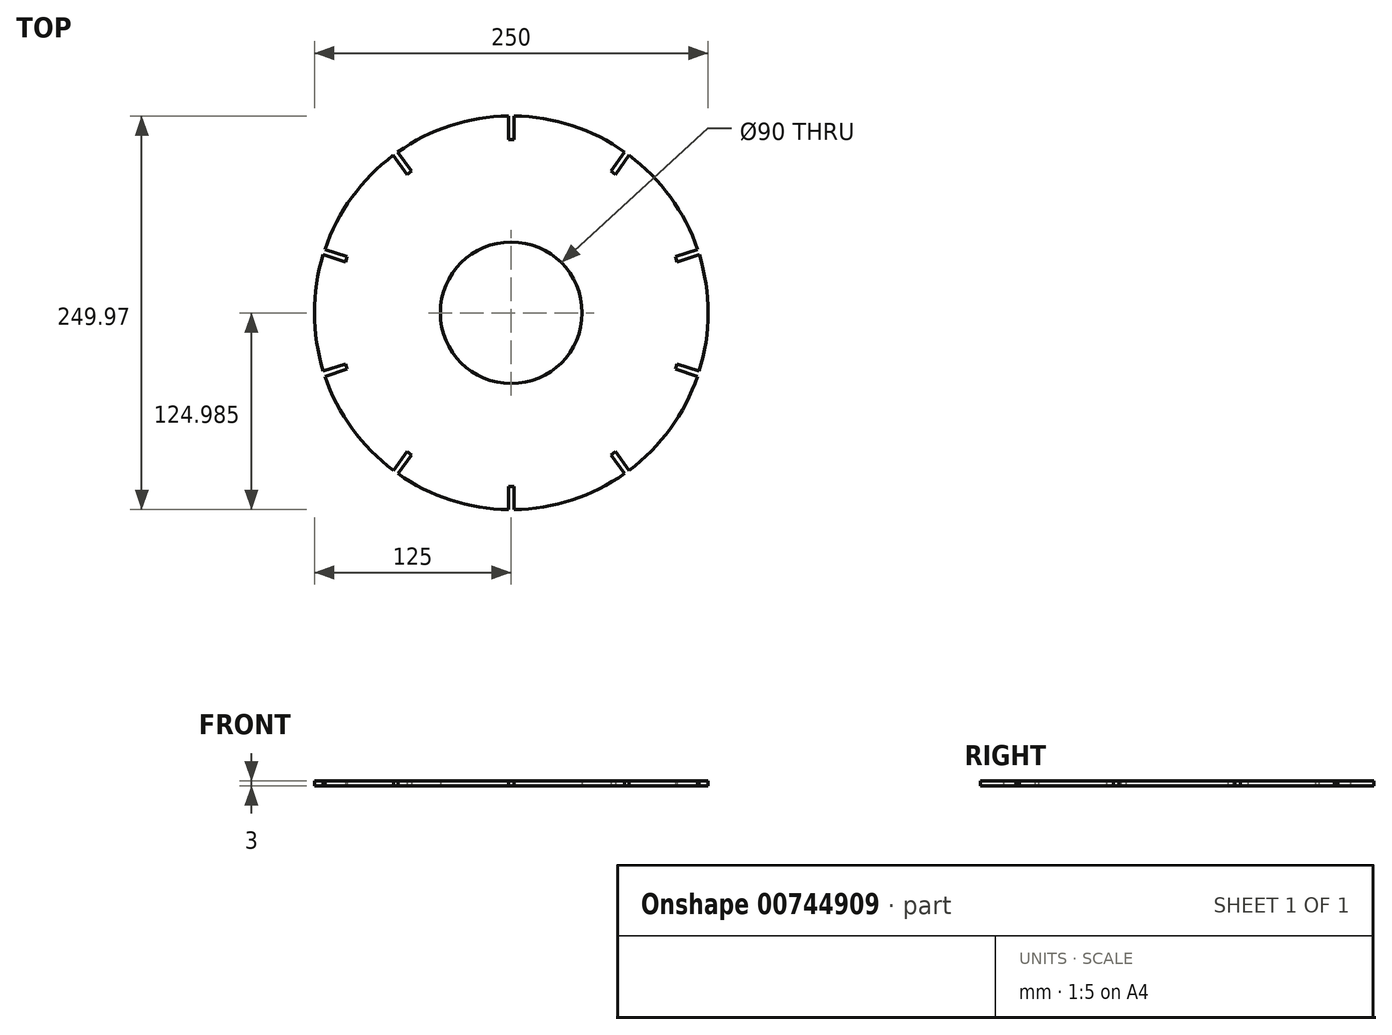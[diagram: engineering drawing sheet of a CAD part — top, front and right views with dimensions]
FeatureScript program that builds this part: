
annotation { "Feature Type Name" : "Feature", "Feature Type Description" : "" }
export const myFeature = defineFeature(function(context is Context, id is Id, definition is map)
    precondition{}
    {
        {
            var Q0;
            Q0=qCreatedBy(makeId("Top.planeOp"),FACE);
            var sketch = newSketch(context, id + "F0", { "sketchPlane" : qUnion([Q0])});
            skCircle(sketch, "E0", {"center": v(0, 0.12) * mm, "radius": 45 * mm});
            skCircle(sketch, "E1", {"center": v(0, 0.12) * mm, "radius": 125 * mm});
            skLineSegment(sketch, "E2.bottom", {"start": v(1.75, 110.12) * mm, "end": v(-1.75, 110.12) * mm});
            skLineSegment(sketch, "E2.top", {"start": v(1.75, 140.12) * mm, "end": v(-1.75, 140.12) * mm});
            skLineSegment(sketch, "E2.left", {"start": v(1.75, 110.12) * mm, "end": v(1.75, 140.12) * mm});
            skLineSegment(sketch, "E2.right", {"start": v(-1.75, 110.12) * mm, "end": v(-1.75, 140.12) * mm});
            skPoint(sketch, "E2.middle", {"position": v(0, 125.12) * mm});
            skPoint(sketch, "E3.center", {"position": v(0, 0) * mm});
            skLineSegment(sketch, "E4.1.0", {"start": v(-66.14, 88.06) * mm, "end": v(-83.77, 112.33) * mm});
            skLineSegment(sketch, "E4.1.1", {"start": v(-63.3, 90.11) * mm, "end": v(-80.94, 114.38) * mm});
            skLineSegment(sketch, "E4.1.2", {"start": v(-63.3, 90.11) * mm, "end": v(-66.14, 88.06) * mm});
            skLineSegment(sketch, "E4.1.3", {"start": v(-80.94, 114.38) * mm, "end": v(-83.77, 112.33) * mm});
            skLineSegment(sketch, "E4.2.0", {"start": v(-105.27, 32.36) * mm, "end": v(-133.8, 41.63) * mm});
            skLineSegment(sketch, "E4.2.1", {"start": v(-104.18, 35.7) * mm, "end": v(-132.72, 44.96) * mm});
            skLineSegment(sketch, "E4.2.2", {"start": v(-104.18, 35.7) * mm, "end": v(-105.27, 32.36) * mm});
            skLineSegment(sketch, "E4.2.3", {"start": v(-132.72, 44.96) * mm, "end": v(-133.8, 41.63) * mm});
            skLineSegment(sketch, "E4.3.0", {"start": v(-104.18, -35.7) * mm, "end": v(-132.72, -44.96) * mm});
            skLineSegment(sketch, "E4.3.1", {"start": v(-105.27, -32.36) * mm, "end": v(-133.8, -41.63) * mm});
            skLineSegment(sketch, "E4.3.2", {"start": v(-105.27, -32.36) * mm, "end": v(-104.18, -35.7) * mm});
            skLineSegment(sketch, "E4.3.3", {"start": v(-133.8, -41.63) * mm, "end": v(-132.72, -44.96) * mm});
            skLineSegment(sketch, "E4.4.0", {"start": v(-63.3, -90.11) * mm, "end": v(-80.94, -114.38) * mm});
            skLineSegment(sketch, "E4.4.1", {"start": v(-66.14, -88.06) * mm, "end": v(-83.77, -112.33) * mm});
            skLineSegment(sketch, "E4.4.2", {"start": v(-66.14, -88.06) * mm, "end": v(-63.3, -90.11) * mm});
            skLineSegment(sketch, "E4.4.3", {"start": v(-83.77, -112.33) * mm, "end": v(-80.94, -114.38) * mm});
            skLineSegment(sketch, "E4.5.0", {"start": v(1.75, -110.12) * mm, "end": v(1.75, -140.12) * mm});
            skLineSegment(sketch, "E4.5.1", {"start": v(-1.75, -110.12) * mm, "end": v(-1.75, -140.12) * mm});
            skLineSegment(sketch, "E4.5.2", {"start": v(-1.75, -110.12) * mm, "end": v(1.75, -110.12) * mm});
            skLineSegment(sketch, "E4.5.3", {"start": v(-1.75, -140.12) * mm, "end": v(1.75, -140.12) * mm});
            skLineSegment(sketch, "E4.6.0", {"start": v(66.14, -88.06) * mm, "end": v(83.77, -112.33) * mm});
            skLineSegment(sketch, "E4.6.1", {"start": v(63.3, -90.11) * mm, "end": v(80.94, -114.38) * mm});
            skLineSegment(sketch, "E4.6.2", {"start": v(63.3, -90.11) * mm, "end": v(66.14, -88.06) * mm});
            skLineSegment(sketch, "E4.6.3", {"start": v(80.94, -114.38) * mm, "end": v(83.77, -112.33) * mm});
            skLineSegment(sketch, "E4.7.0", {"start": v(105.27, -32.36) * mm, "end": v(133.8, -41.63) * mm});
            skLineSegment(sketch, "E4.7.1", {"start": v(104.18, -35.7) * mm, "end": v(132.72, -44.96) * mm});
            skLineSegment(sketch, "E4.7.2", {"start": v(104.18, -35.7) * mm, "end": v(105.27, -32.36) * mm});
            skLineSegment(sketch, "E4.7.3", {"start": v(132.72, -44.96) * mm, "end": v(133.8, -41.63) * mm});
            skLineSegment(sketch, "E4.8.0", {"start": v(104.18, 35.7) * mm, "end": v(132.72, 44.96) * mm});
            skLineSegment(sketch, "E4.8.1", {"start": v(105.27, 32.36) * mm, "end": v(133.8, 41.63) * mm});
            skLineSegment(sketch, "E4.8.2", {"start": v(105.27, 32.36) * mm, "end": v(104.18, 35.7) * mm});
            skLineSegment(sketch, "E4.8.3", {"start": v(133.8, 41.63) * mm, "end": v(132.72, 44.96) * mm});
            skLineSegment(sketch, "E4.9.0", {"start": v(63.3, 90.11) * mm, "end": v(80.94, 114.38) * mm});
            skLineSegment(sketch, "E4.9.1", {"start": v(66.14, 88.06) * mm, "end": v(83.77, 112.33) * mm});
            skLineSegment(sketch, "E4.9.2", {"start": v(66.14, 88.06) * mm, "end": v(63.3, 90.11) * mm});
            skLineSegment(sketch, "E4.9.3", {"start": v(83.77, 112.33) * mm, "end": v(80.94, 114.38) * mm});
            skSolve(sketch);
        }
        {
            var Q0;
            Q0=makeQuery(id+"F0.imprint","IMPRINT",FACE,{"disambiguationData":[TD([[makeQuery(id+"F0.imprint","IMPRINT",EDGE,{"derivedFrom":sQuery(id+"F0.wireOp",EDGE,"E0")}),-1.0]])]});
            extrude(context, id + "F1", {"entities" : qUnion([Q0]), "depth" : 3 * mm, "offsetDistance" : 25 * mm});
        }
        {
            var Q0;
            Q0=makeQuery(id+"F0.imprint","IMPRINT",FACE,{"disambiguationData":[TD([[makeQuery(id+"F0.imprint","IMPRINT",EDGE,{"derivedFrom":sQuery(id+"F0.wireOp",EDGE,"E0")}),-1.0]])]});
            extrude(context, id + "F2", {"entities" : qUnion([Q0]), "operationType" : NewBodyOperationType.ADD, "depth" : 3 * mm, "offsetDistance" : 25 * mm});
        }
    });
